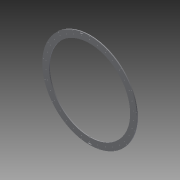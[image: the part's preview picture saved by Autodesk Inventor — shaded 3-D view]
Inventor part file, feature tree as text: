
AUTODESK INVENTOR PART (.ipt)
format: ipt  version: 2013 (Build 170138000, 138)  size: 203,264 bytes
history: native  units: in
note: dims shown in document units (in); Inventor stores cm internally (conversion verified against a paired STEP export)
features: extrude x1, sketch x1
ambient origin geometry x8: Origin, YZ Plane, XZ Plane, XY Plane, X Axis, Y Axis, Z Axis, Center Point
bodies: Solid1 (feature_tree)
feature tree (2):
  extrude  "Extrusion1"  Depth=24.0in
  sketch  "Sketch1"  dims[d1=28.0in d3=24.0in d6=0.25in d7=0.25in d8=6.6929in d10=360.0deg d13=0.25in d15=0.13in d16=6.6929in d18=360.0deg d20=13.5in d21=0.5in d22=0.25in d23=1.0in d24=0.7874in d26=360.0deg d28=0.25in d29=0.0in]
